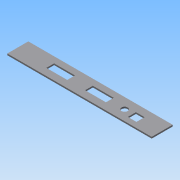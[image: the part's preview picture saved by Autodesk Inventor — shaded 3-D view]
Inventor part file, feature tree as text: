
AUTODESK INVENTOR PART (.ipt)
format: ipt  version: 2013 (Build 170138000, 138)  size: 111,104 bytes
history: native  units: mm
features: extrude x1, sketch x1
ambient origin geometry x8: Origin, YZ Plane, XZ Plane, XY Plane, X Axis, Y Axis, Z Axis, Center Point
bodies: Solid1 (feature_tree)
feature tree (2):
  extrude  "Extrusion1"  Depth=1.9mm TaperAngle=0.0deg
  sketch  "Sketch1"  dims[d1=6.75mm d2=7.9mm d3=24.6mm d4=3.3mm d5=3.3mm d6=24.6mm d7=7.9mm d8=24.8mm d10=6.0mm d11=6.5mm d12=20.6mm d13=9.0mm d14=1.1mm d15=8.4mm d17=1.0mm d18=1.0mm d19=1.0mm d20=1.0mm d21=1.9mm d22=0.0mm d27=11.5mm d30=26.8mm d32=41.8mm d33=184.2mm]
